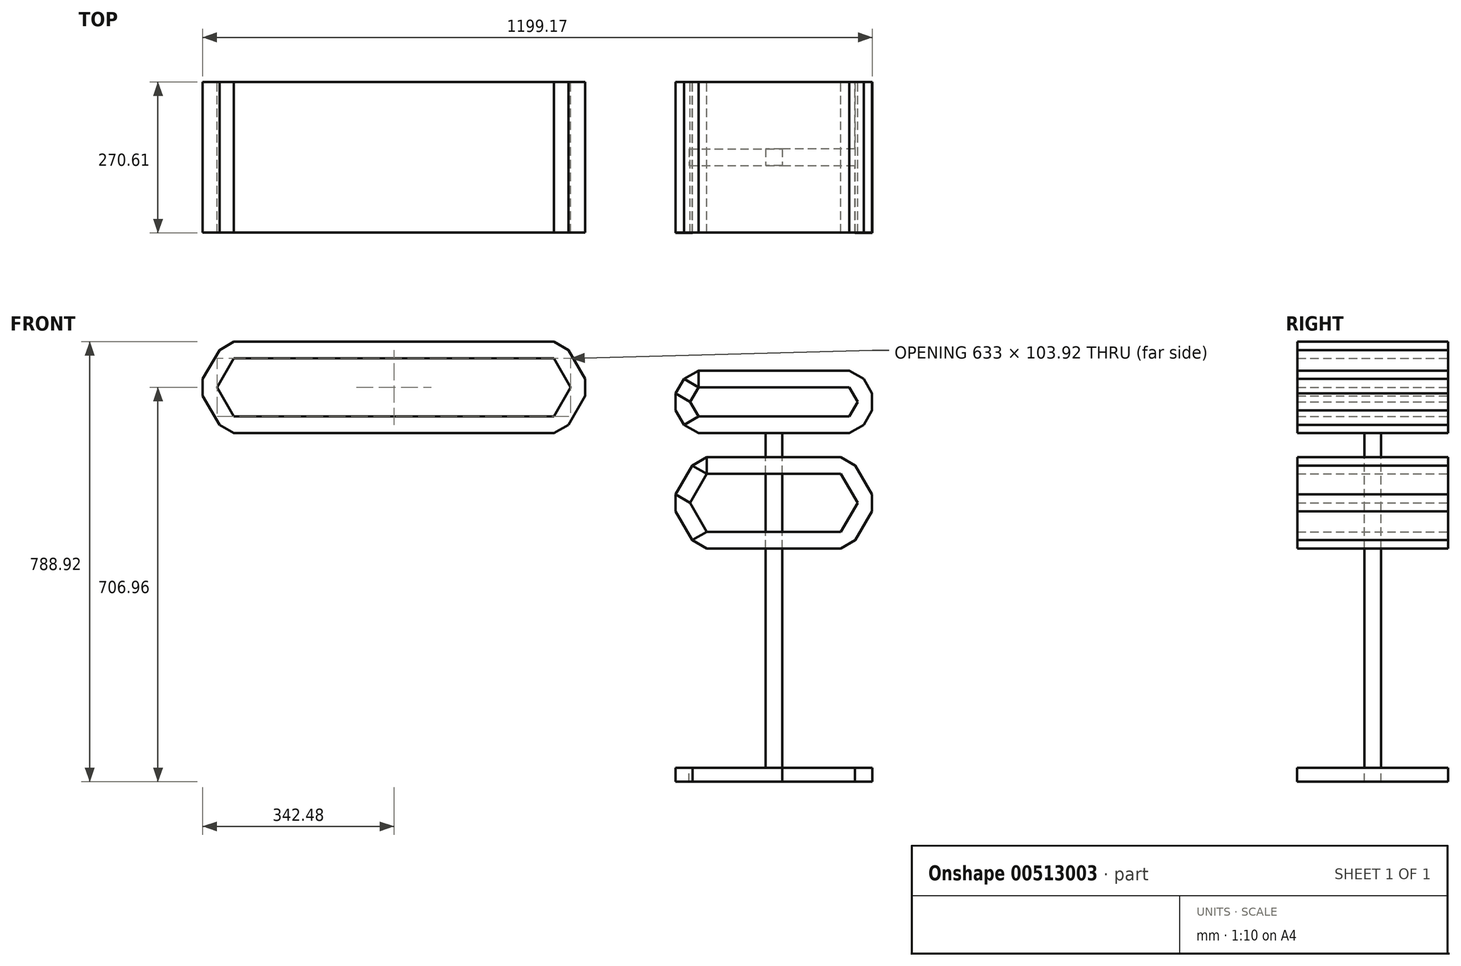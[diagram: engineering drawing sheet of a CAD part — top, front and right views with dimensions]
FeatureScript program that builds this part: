
annotation { "Feature Type Name" : "Feature", "Feature Type Description" : "" }
export const myFeature = defineFeature(function(context is Context, id is Id, definition is map)
    precondition{}
    {
        {
            var Q0;
            Q0=qCreatedBy(makeId("Front.planeOp"),FACE);
            var sketch = newSketch(context, id + "F0", { "sketchPlane" : qUnion([Q0])});
            skLineSegment(sketch, "E0.0", {"start": v(295.98, -66.96) * mm, "end": v(270, -81.96) * mm});
            skLineSegment(sketch, "E0.3", {"start": v(-10.98, -273.94) * mm, "end": v(-40.98, -221.98) * mm});
            skLineSegment(sketch, "E0.4", {"start": v(-40.98, -221.98) * mm, "end": v(-40.98, -191.98) * mm});
            skLineSegment(sketch, "E0.5", {"start": v(-40.98, -10.98) * mm, "end": v(-25.98, 15) * mm});
            skLineSegment(sketch, "E0.6", {"start": v(-10.98, -140.02) * mm, "end": v(15, -125.02) * mm});
            skLineSegment(sketch, "E0.9", {"start": v(295.98, 15) * mm, "end": v(310.98, -10.98) * mm});
            skLineSegment(sketch, "E0.10", {"start": v(310.98, -10.98) * mm, "end": v(310.98, -40.98) * mm});
            skLineSegment(sketch, "E0.11", {"start": v(310.98, -40.98) * mm, "end": v(295.98, -66.96) * mm});
            skLineSegment(sketch, "E1.bottom", {"start": v(-25.98, 15) * mm, "end": v(0, 0) * mm});
            skLineSegment(sketch, "E1.top", {"start": v(-40.98, -10.98) * mm, "end": v(-15, -25.98) * mm});
            skLineSegment(sketch, "E1.left", {"start": v(-10.98, -140.02) * mm, "end": v(-40.98, -191.98) * mm});
            skLineSegment(sketch, "E1.right", {"start": v(0, 0) * mm, "end": v(-15, -25.98) * mm});
            skLineSegment(sketch, "E2", {"start": v(0, 0) * mm, "end": v(0, 30) * mm});
            skLineSegment(sketch, "E3", {"start": v(270, 0) * mm, "end": v(270, 30) * mm});
            skLineSegment(sketch, "E4", {"start": v(270, 0) * mm, "end": v(295.98, 15) * mm});
            skLineSegment(sketch, "E5", {"start": v(270, 0) * mm, "end": v(285, -25.98) * mm});
            skLineSegment(sketch, "E6", {"start": v(310.98, -10.98) * mm, "end": v(285, -25.98) * mm});
            skLineSegment(sketch, "E7", {"start": v(285, -25.98) * mm, "end": v(310.98, -40.98) * mm});
            skLineSegment(sketch, "E8", {"start": v(285, -25.98) * mm, "end": v(270, -51.96) * mm});
            skLineSegment(sketch, "E9", {"start": v(270, -51.96) * mm, "end": v(295.98, -66.96) * mm});
            skLineSegment(sketch, "E10", {"start": v(270, -51.96) * mm, "end": v(270, -81.96) * mm});
            skLineSegment(sketch, "E11", {"start": v(0, -51.96) * mm, "end": v(0, -81.96) * mm});
            skLineSegment(sketch, "E12", {"start": v(0, -51.96) * mm, "end": v(-25.98, -66.96) * mm});
            skLineSegment(sketch, "E13", {"start": v(-40.98, -40.98) * mm, "end": v(-15, -25.98) * mm});
            skLineSegment(sketch, "E14", {"start": v(-15, -25.98) * mm, "end": v(0, -51.96) * mm});
            skLineSegment(sketch, "E15.0", {"start": v(270, -51.96) * mm, "end": v(295.98, -66.96) * mm, "construction": true});
            skLineSegment(sketch, "E16.0", {"start": v(-40.98, -10.98) * mm, "end": v(-15, -25.98) * mm, "construction": true});
            skLineSegment(sketch, "E17", {"start": v(270, 30) * mm, "end": v(295.98, 15) * mm});
            skLineSegment(sketch, "E18", {"start": v(-10.98, -273.94) * mm, "end": v(15, -288.94) * mm});
            skLineSegment(sketch, "E19", {"start": v(0, -81.96) * mm, "end": v(270, -81.96) * mm});
            skLineSegment(sketch, "E20", {"start": v(0, 0) * mm, "end": v(270, 0) * mm});
            skLineSegment(sketch, "E21", {"start": v(270, 30) * mm, "end": v(0, 30) * mm});
            skLineSegment(sketch, "E22", {"start": v(270, -51.96) * mm, "end": v(240, -51.96) * mm});
            skLineSegment(sketch, "E23", {"start": v(240, -51.96) * mm, "end": v(210, -51.96) * mm});
            skLineSegment(sketch, "E24", {"start": v(210, -51.96) * mm, "end": v(180, -51.96) * mm});
            skLineSegment(sketch, "E25", {"start": v(180, -51.96) * mm, "end": v(150, -51.96) * mm});
            skLineSegment(sketch, "E26", {"start": v(150, -51.96) * mm, "end": v(120, -51.96) * mm});
            skLineSegment(sketch, "E27", {"start": v(120, -51.96) * mm, "end": v(90, -51.96) * mm});
            skLineSegment(sketch, "E28", {"start": v(90, -51.96) * mm, "end": v(60, -51.96) * mm});
            skLineSegment(sketch, "E29", {"start": v(60, -51.96) * mm, "end": v(30, -51.96) * mm});
            skLineSegment(sketch, "E30", {"start": v(30, -51.96) * mm, "end": v(0, -51.96) * mm});
            skLineSegment(sketch, "E31.bottom", {"start": v(120, -51.96) * mm, "end": v(120, -51.96) * mm});
            skLineSegment(sketch, "E31.top", {"start": v(120, -81.96) * mm, "end": v(120, -81.96) * mm});
            skLineSegment(sketch, "E31.left", {"start": v(120, -51.96) * mm, "end": v(120, -81.96) * mm});
            skLineSegment(sketch, "E31.right", {"start": v(120, -51.96) * mm, "end": v(120, -81.96) * mm});
            skLineSegment(sketch, "E32.bottom", {"start": v(150, -51.96) * mm, "end": v(150, -51.96) * mm});
            skLineSegment(sketch, "E32.top", {"start": v(150, -81.96) * mm, "end": v(150, -81.96) * mm});
            skLineSegment(sketch, "E32.left", {"start": v(150, -51.96) * mm, "end": v(150, -81.96) * mm});
            skLineSegment(sketch, "E32.right", {"start": v(150, -51.96) * mm, "end": v(150, -81.96) * mm});
            skLineSegment(sketch, "E33", {"start": v(120, -66.96) * mm, "end": v(150, -66.96) * mm});
            skLineSegment(sketch, "E34.top", {"start": v(120, -81.96) * mm, "end": v(150, -81.96) * mm});
            skLineSegment(sketch, "E35", {"start": v(135, -81.96) * mm, "end": v(135, -389.53) * mm});
            skLineSegment(sketch, "E36", {"start": v(-40.98, -191.98) * mm, "end": v(-15, -206.98) * mm});
            skLineSegment(sketch, "E37", {"start": v(-10.98, -140.02) * mm, "end": v(15, -155.02) * mm});
            skLineSegment(sketch, "E38", {"start": v(15, -155.02) * mm, "end": v(15, -125.02) * mm});
            skLineSegment(sketch, "E39", {"start": v(15, -155.02) * mm, "end": v(-15, -206.98) * mm});
            skLineSegment(sketch, "E40", {"start": v(-40.98, -221.98) * mm, "end": v(-15, -206.98) * mm});
            skLineSegment(sketch, "E41", {"start": v(-10.98, -273.94) * mm, "end": v(15, -258.94) * mm});
            skLineSegment(sketch, "E42", {"start": v(15, -288.94) * mm, "end": v(15, -258.94) * mm});
            skLineSegment(sketch, "E43", {"start": v(15, -258.94) * mm, "end": v(-15, -206.98) * mm});
            skLineSegment(sketch, "E44", {"start": v(0, 30) * mm, "end": v(-25.98, 15) * mm});
            skLineSegment(sketch, "E45", {"start": v(-40.98, -10.98) * mm, "end": v(-40.98, -40.98) * mm});
            skLineSegment(sketch, "E46", {"start": v(-40.98, -40.98) * mm, "end": v(-25.98, -66.96) * mm});
            skLineSegment(sketch, "E47", {"start": v(-25.98, -66.96) * mm, "end": v(0, -81.96) * mm});
            skLineSegment(sketch, "E48.MirrorCS", {"start": v(280.98, -140.02) * mm, "end": v(255, -125.02) * mm});
            skLineSegment(sketch, "E49.MirrorCS", {"start": v(255, -155.02) * mm, "end": v(255, -125.02) * mm});
            skLineSegment(sketch, "E50.MirrorCS", {"start": v(255, -258.94) * mm, "end": v(285, -206.98) * mm});
            skLineSegment(sketch, "E51.MirrorCS", {"start": v(280.98, -273.94) * mm, "end": v(255, -258.94) * mm});
            skLineSegment(sketch, "E52.MirrorCS", {"start": v(280.98, -140.02) * mm, "end": v(255, -155.02) * mm});
            skLineSegment(sketch, "E53.MirrorCS", {"start": v(310.98, -221.98) * mm, "end": v(285, -206.98) * mm});
            skLineSegment(sketch, "E54.MirrorCS", {"start": v(310.98, -191.98) * mm, "end": v(285, -206.98) * mm});
            skLineSegment(sketch, "E55.MirrorCS", {"start": v(280.98, -273.94) * mm, "end": v(255, -288.94) * mm});
            skLineSegment(sketch, "E56.MirrorCS", {"start": v(280.98, -273.94) * mm, "end": v(310.98, -221.98) * mm});
            skLineSegment(sketch, "E57.MirrorCS", {"start": v(280.98, -140.02) * mm, "end": v(310.98, -191.98) * mm});
            skLineSegment(sketch, "E58.MirrorCS", {"start": v(255, -288.94) * mm, "end": v(255, -258.94) * mm});
            skLineSegment(sketch, "E59.MirrorCS", {"start": v(310.98, -221.98) * mm, "end": v(310.98, -191.98) * mm});
            skLineSegment(sketch, "E60.MirrorCS", {"start": v(255, -155.02) * mm, "end": v(285, -206.98) * mm});
            skLineSegment(sketch, "E61", {"start": v(15, -155.02) * mm, "end": v(255, -155.02) * mm});
            skLineSegment(sketch, "E62", {"start": v(15, -125.02) * mm, "end": v(255, -125.02) * mm});
            skLineSegment(sketch, "E63", {"start": v(15, -258.94) * mm, "end": v(255, -258.94) * mm});
            skLineSegment(sketch, "E64", {"start": v(15, -288.94) * mm, "end": v(255, -288.94) * mm});
            skLineSegment(sketch, "E65.3", {"start": v(-857.98, -66.96) * mm, "end": v(-887.98, -15) * mm});
            skLineSegment(sketch, "E65.4", {"start": v(-887.98, -15) * mm, "end": v(-887.98, 15) * mm});
            skLineSegment(sketch, "E65.6", {"start": v(-857.98, 66.96) * mm, "end": v(-832, 81.96) * mm});
            skLineSegment(sketch, "E66.left", {"start": v(-857.98, 66.96) * mm, "end": v(-887.98, 15) * mm});
            skLineSegment(sketch, "E67", {"start": v(-857.98, -66.96) * mm, "end": v(-832, -81.96) * mm});
            skLineSegment(sketch, "E68", {"start": v(-887.98, 15) * mm, "end": v(-862, 0) * mm});
            skLineSegment(sketch, "E69", {"start": v(-857.98, 66.96) * mm, "end": v(-832, 51.96) * mm});
            skLineSegment(sketch, "E70", {"start": v(-832, 51.96) * mm, "end": v(-832, 81.96) * mm});
            skLineSegment(sketch, "E71", {"start": v(-832, 51.96) * mm, "end": v(-862, 0) * mm});
            skLineSegment(sketch, "E72", {"start": v(-887.98, -15) * mm, "end": v(-862, 0) * mm});
            skLineSegment(sketch, "E73", {"start": v(-857.98, -66.96) * mm, "end": v(-832, -51.96) * mm});
            skLineSegment(sketch, "E74", {"start": v(-832, -81.96) * mm, "end": v(-832, -51.96) * mm});
            skLineSegment(sketch, "E75", {"start": v(-832, -51.96) * mm, "end": v(-862, 0) * mm});
            skLineSegment(sketch, "E76.MirrorCS", {"start": v(-233.02, 66.96) * mm, "end": v(-259, 81.96) * mm});
            skLineSegment(sketch, "E77.MirrorCS", {"start": v(-259, 51.96) * mm, "end": v(-259, 81.96) * mm});
            skLineSegment(sketch, "E78.MirrorCS", {"start": v(-259, -51.96) * mm, "end": v(-229, 0) * mm});
            skLineSegment(sketch, "E79.MirrorCS", {"start": v(-233.02, -66.96) * mm, "end": v(-259, -51.96) * mm});
            skLineSegment(sketch, "E80.MirrorCS", {"start": v(-233.02, 66.96) * mm, "end": v(-259, 51.96) * mm});
            skLineSegment(sketch, "E81.MirrorCS", {"start": v(-203.02, -15) * mm, "end": v(-229, 0) * mm});
            skLineSegment(sketch, "E82.MirrorCS", {"start": v(-203.02, 15) * mm, "end": v(-229, 0) * mm});
            skLineSegment(sketch, "E83.MirrorCS", {"start": v(-233.02, -66.96) * mm, "end": v(-259, -81.96) * mm});
            skLineSegment(sketch, "E84.MirrorCS", {"start": v(-233.02, -66.96) * mm, "end": v(-203.02, -15) * mm});
            skLineSegment(sketch, "E85.MirrorCS", {"start": v(-233.02, 66.96) * mm, "end": v(-203.02, 15) * mm});
            skLineSegment(sketch, "E86.MirrorCS", {"start": v(-259, -81.96) * mm, "end": v(-259, -51.96) * mm});
            skLineSegment(sketch, "E87.MirrorCS", {"start": v(-203.02, -15) * mm, "end": v(-203.02, 15) * mm});
            skLineSegment(sketch, "E88.MirrorCS", {"start": v(-259, 51.96) * mm, "end": v(-229, 0) * mm});
            skLineSegment(sketch, "E89", {"start": v(-259, 81.96) * mm, "end": v(-832, 81.96) * mm});
            skLineSegment(sketch, "E90", {"start": v(-832, 51.96) * mm, "end": v(-259, 51.96) * mm});
            skLineSegment(sketch, "E91", {"start": v(-832, -51.96) * mm, "end": v(-259, -51.96) * mm});
            skLineSegment(sketch, "E92", {"start": v(-832, -81.96) * mm, "end": v(-259, -81.96) * mm});
            skSolve(sketch);
        }
        {
            var Q0;
            Q0=qCreatedBy(makeId("Front.planeOp"),FACE);
            var sketch = newSketch(context, id + "F1", { "sketchPlane" : qUnion([Q0])});
            skSolve(sketch);
        }
        {
            var Q0;
            Q0=makeQuery(id+"F0.imprint","IMPRINT",FACE,{"disambiguationData":[TD([[makeQuery(id+"F0.imprint","IMPRINT",EDGE,{"derivedFrom":sQuery(id+"F0.wireOp",EDGE,"E0.0")}),-1.0]])]});
            var Q1;
            Q1=makeQuery(id+"F0.imprint","IMPRINT",FACE,{"disambiguationData":[TD([[makeQuery(id+"F0.imprint","IMPRINT",EDGE,{"derivedFrom":sQuery(id+"F0.wireOp",EDGE,"E3")}),-1.0]])]});
            var Q2;
            {var subQ4=sQuery(id+"F0.wireOp",EDGE,"E10");Q2=makeQuery(id+"F0.imprint","IMPRINT",FACE,{"disambiguationData":[TD([[makeQuery(id+"F0.imprint","IMPRINT",EDGE,{"derivedFrom":subQ4}),-1.0]])]});}
            var Q3;
            {var subQ0=sQuery(id+"F0.wireOp",EDGE,"E26");Q3=makeQuery(id+"F0.imprint","IMPRINT",FACE,{"disambiguationData":[TD([[makeQuery(id+"F0.imprint","IMPRINT",EDGE,{"derivedFrom":subQ0}),1.0]])]});}
            var Q4;
            Q4=makeQuery(id+"F0.imprint","IMPRINT",FACE,{"disambiguationData":[TD([[makeQuery(id+"F0.imprint","IMPRINT",EDGE,{"derivedFrom":sQuery(id+"F0.wireOp",EDGE,"E0.3")}),-1.0]])]});
            var Q5;
            Q5=makeQuery(id+"F0.imprint","IMPRINT",FACE,{"disambiguationData":[TD([[makeQuery(id+"F0.imprint","IMPRINT",EDGE,{"derivedFrom":sQuery(id+"F0.wireOp",EDGE,"E0.10")}),-1.0]])]});
            var Q6;
            Q6=makeQuery(id+"F0.imprint","IMPRINT",FACE,{"disambiguationData":[TD([[makeQuery(id+"F0.imprint","IMPRINT",EDGE,{"derivedFrom":sQuery(id+"F0.wireOp",EDGE,"E0.4")}),-1.0]])]});
            var Q7;
            {var subQ1=sQuery(id+"F0.wireOp",EDGE,"E11");Q7=makeQuery(id+"F0.imprint","IMPRINT",FACE,{"disambiguationData":[TD([[makeQuery(id+"F0.imprint","IMPRINT",EDGE,{"derivedFrom":subQ1}),1.0]])]});}
            var Q8;
            {var subQ3=sQuery(id+"F0.wireOp",EDGE,"E33");Q8=makeQuery(id+"F0.imprint","IMPRINT",FACE,{"disambiguationData":[TD([[makeQuery(id+"F0.imprint","IMPRINT",EDGE,{"derivedFrom":subQ3}),-1.0]])]});}
            var Q9;
            Q9=makeQuery(id+"F0.imprint","IMPRINT",FACE,{"disambiguationData":[TD([[makeQuery(id+"F0.imprint","IMPRINT",EDGE,{"derivedFrom":sQuery(id+"F0.wireOp",EDGE,"E0.11")}),-1.0]])]});
            var Q10;
            Q10=makeQuery(id+"F0.imprint","IMPRINT",FACE,{"disambiguationData":[TD([[makeQuery(id+"F0.imprint","IMPRINT",EDGE,{"derivedFrom":sQuery(id+"F0.wireOp",EDGE,"E11")}),-1.0]])]});
            var Q11;
            Q11=makeQuery(id+"F0.imprint","IMPRINT",FACE,{"disambiguationData":[TD([[makeQuery(id+"F0.imprint","IMPRINT",EDGE,{"derivedFrom":sQuery(id+"F0.wireOp",EDGE,"E0.9")}),-1.0]])]});
            var Q12;
            Q12=makeQuery(id+"F0.imprint","IMPRINT",FACE,{"disambiguationData":[TD([[makeQuery(id+"F0.imprint","IMPRINT",EDGE,{"derivedFrom":sQuery(id+"F0.wireOp",EDGE,"E2")}),-1.0]])]});
            var Q13;
            Q13=makeQuery(id+"F0.imprint","IMPRINT",FACE,{"disambiguationData":[TD([[makeQuery(id+"F0.imprint","IMPRINT",EDGE,{"derivedFrom":sQuery(id+"F0.wireOp",EDGE,"E1.bottom")}),-1.0]])]});
            var Q14;
            Q14=makeQuery(id+"F0.imprint","IMPRINT",FACE,{"disambiguationData":[TD([[makeQuery(id+"F0.imprint","IMPRINT",EDGE,{"derivedFrom":sQuery(id+"F0.wireOp",EDGE,"E0.6")}),-1.0]])]});
            var Q15;
            Q15 = qSketchRegion(id + "F1", true);
            extrude(context, id + "F2", {"entities" : qUnion([Q0, Q1, Q2, Q3, Q4, Q5, Q6, Q7, Q8, Q9, Q10, Q11, Q12, Q13, Q14, Q15]), "depth" : 270 * mm});
        }
        {
            var Q0;
            Q0=makeQuery(id+"F2.opExtrude","SWEPT_FACE",FACE,{"disambiguationData":[OSD([sQuery(id+"F0.wireOp",EDGE,"E19"),sQuery(id+"F0.wireOp",EDGE,"E34.top")])]});
            var sketch = newSketch(context, id + "F3", { "sketchPlane" : qUnion([Q0])});
            skPoint(sketch, "E93.startSnap0", {"position": v(135, 270) * mm});
            skLineSegment(sketch, "E94.bottom", {"start": v(150, 120) * mm, "end": v(120, 120) * mm});
            skLineSegment(sketch, "E94.top", {"start": v(150, 150) * mm, "end": v(120, 150) * mm});
            skLineSegment(sketch, "E94.left", {"start": v(150, 120) * mm, "end": v(150, 150) * mm});
            skLineSegment(sketch, "E94.right", {"start": v(120, 120) * mm, "end": v(120, 150) * mm});
            skPoint(sketch, "E94.middle", {"position": v(135, 135) * mm});
            skSolve(sketch);
        }
        {
            var Q0;
            Q0=makeQuery(id+"F3.imprint","IMPRINT",FACE,{"disambiguationData":[TD([[makeQuery(id+"F3.imprint","IMPRINT",EDGE,{"derivedFrom":sQuery(id+"F3.wireOp",EDGE,"E94.bottom")}),-1.0]])]});
            extrude(context, id + "F4", {"entities" : qUnion([Q0]), "operationType" : NewBodyOperationType.ADD, "depth" : 600 * mm});
        }
        {
            var Q0;
            Q0=makeQuery(id+"F4.opExtrude","CAP_FACE",FACE,{"disambiguationData":[OSD([sQuery(id+"F3.wireOp",EDGE,"E94.bottom"),sQuery(id+"F3.wireOp",EDGE,"E94.top"),sQuery(id+"F3.wireOp",EDGE,"E94.left"),sQuery(id+"F3.wireOp",EDGE,"E94.right")])],"isStart":false});
            var sketch = newSketch(context, id + "F5", { "sketchPlane" : qUnion([Q0])});
            skLineSegment(sketch, "E95", {"start": v(120, 150) * mm, "end": v(-41.14, 150) * mm});
            skLineSegment(sketch, "E96", {"start": v(-41.14, 150) * mm, "end": v(-41.14, 270.6) * mm});
            skLineSegment(sketch, "E97", {"start": v(-41.14, 270.6) * mm, "end": v(-10.86, 270.6) * mm});
            skLineSegment(sketch, "E98", {"start": v(-10.86, 270.6) * mm, "end": v(-10.86, 0) * mm});
            skLineSegment(sketch, "E99", {"start": v(-10.86, 0) * mm, "end": v(-41.14, 0) * mm});
            skLineSegment(sketch, "E100", {"start": v(-41.14, 0) * mm, "end": v(-41.14, 150) * mm});
            skLineSegment(sketch, "E101", {"start": v(120, 120) * mm, "end": v(-41.14, 120) * mm});
            skLineSegment(sketch, "E102", {"start": v(-41.14, 120) * mm, "end": v(-41.14, 150) * mm});
            skLineSegment(sketch, "E103", {"start": v(150, 150) * mm, "end": v(311.19, 150) * mm});
            skLineSegment(sketch, "E104", {"start": v(311.19, 150) * mm, "end": v(311.19, 270.6) * mm});
            skLineSegment(sketch, "E105", {"start": v(311.19, 270.6) * mm, "end": v(280, 270.6) * mm});
            skLineSegment(sketch, "E106", {"start": v(280, 270.6) * mm, "end": v(280, 0) * mm});
            skLineSegment(sketch, "E107", {"start": v(280, 0) * mm, "end": v(311.19, 0) * mm});
            skLineSegment(sketch, "E108", {"start": v(311.19, 0) * mm, "end": v(311.19, 150) * mm});
            skLineSegment(sketch, "E109", {"start": v(311.19, 120) * mm, "end": v(150, 120) * mm});
            skLineSegment(sketch, "E110", {"start": v(150, 120) * mm, "end": v(150, 150) * mm});
            skSolve(sketch);
        }
        {
            var Q0;
            Q0 = qSketchRegion(id + "F5", true);
            extrude(context, id + "F6", {"entities" : qUnion([Q0]), "depth" : 25 * mm});
        }
        {
            var Q0;
            Q0=makeQuery(id+"F6.opExtrude","SWEPT_FACE",FACE,{"disambiguationData":[OSD([sQuery(id+"F5.wireOp",EDGE,"E110")])]});
            extrude(context, id + "F7", {"entities" : qUnion([Q0]), "depth" : 167 * mm});
        }
        {
            var Q0;
            Q0=makeQuery(id+"F0.imprint","IMPRINT",FACE,{"disambiguationData":[TD([[makeQuery(id+"F0.imprint","IMPRINT",EDGE,{"derivedFrom":sQuery(id+"F0.wireOp",EDGE,"E1.bottom")}),1.0]])]});
            var Q1;
            Q1=makeQuery(id+"F0.imprint","IMPRINT",FACE,{"disambiguationData":[TD([[makeQuery(id+"F0.imprint","IMPRINT",EDGE,{"derivedFrom":sQuery(id+"F0.wireOp",EDGE,"E1.top")}),-1.0]])]});
            var Q2;
            Q2=makeQuery(id+"F0.imprint","IMPRINT",FACE,{"disambiguationData":[TD([[makeQuery(id+"F0.imprint","IMPRINT",EDGE,{"derivedFrom":sQuery(id+"F0.wireOp",EDGE,"E12")}),-1.0]])]});
            extrude(context, id + "F8", {"entities" : qUnion([Q0, Q1, Q2]), "depth" : 270 * mm});
        }
        {
            var Q0;
            {var subQ5=sQuery(id+"F0.wireOp",EDGE,"E38");Q0=makeQuery(id+"F0.imprint","IMPRINT",FACE,{"disambiguationData":[TD([[makeQuery(id+"F0.imprint","IMPRINT",EDGE,{"derivedFrom":subQ5}),-1.0]])]});}
            var Q1;
            {var subQ5=sQuery(id+"F0.wireOp",EDGE,"E49.MirrorCS");Q1=makeQuery(id+"F0.imprint","IMPRINT",FACE,{"disambiguationData":[TD([[makeQuery(id+"F0.imprint","IMPRINT",EDGE,{"derivedFrom":subQ5}),1.0]])]});}
            var Q2;
            Q2=makeQuery(id+"F0.imprint","IMPRINT",FACE,{"disambiguationData":[TD([[makeQuery(id+"F0.imprint","IMPRINT",EDGE,{"derivedFrom":sQuery(id+"F0.wireOp",EDGE,"E48.MirrorCS")}),1.0]])]});
            var Q3;
            Q3=makeQuery(id+"F0.imprint","IMPRINT",FACE,{"disambiguationData":[TD([[makeQuery(id+"F0.imprint","IMPRINT",EDGE,{"derivedFrom":sQuery(id+"F0.wireOp",EDGE,"E52.MirrorCS")}),1.0]])]});
            var Q4;
            Q4=makeQuery(id+"F0.imprint","IMPRINT",FACE,{"disambiguationData":[TD([[makeQuery(id+"F0.imprint","IMPRINT",EDGE,{"derivedFrom":sQuery(id+"F0.wireOp",EDGE,"E50.MirrorCS")}),-1.0]])]});
            var Q5;
            {var subQ5=sQuery(id+"F0.wireOp",EDGE,"E58.MirrorCS");Q5=makeQuery(id+"F0.imprint","IMPRINT",FACE,{"disambiguationData":[TD([[makeQuery(id+"F0.imprint","IMPRINT",EDGE,{"derivedFrom":subQ5}),1.0]])]});}
            var Q6;
            {var subQ5=sQuery(id+"F0.wireOp",EDGE,"E42");Q6=makeQuery(id+"F0.imprint","IMPRINT",FACE,{"disambiguationData":[TD([[makeQuery(id+"F0.imprint","IMPRINT",EDGE,{"derivedFrom":subQ5}),-1.0]])]});}
            var Q7;
            Q7=makeQuery(id+"F0.imprint","IMPRINT",FACE,{"disambiguationData":[TD([[makeQuery(id+"F0.imprint","IMPRINT",EDGE,{"derivedFrom":sQuery(id+"F0.wireOp",EDGE,"E1.left")}),1.0]])]});
            var Q8;
            Q8=makeQuery(id+"F0.imprint","IMPRINT",FACE,{"disambiguationData":[TD([[makeQuery(id+"F0.imprint","IMPRINT",EDGE,{"derivedFrom":sQuery(id+"F0.wireOp",EDGE,"E18")}),1.0]])]});
            var Q9;
            Q9=makeQuery(id+"F0.imprint","IMPRINT",FACE,{"disambiguationData":[TD([[makeQuery(id+"F0.imprint","IMPRINT",EDGE,{"derivedFrom":sQuery(id+"F0.wireOp",EDGE,"E51.MirrorCS")}),1.0]])]});
            var Q10;
            Q10=makeQuery(id+"F0.imprint","IMPRINT",FACE,{"disambiguationData":[TD([[makeQuery(id+"F0.imprint","IMPRINT",EDGE,{"derivedFrom":sQuery(id+"F0.wireOp",EDGE,"E53.MirrorCS")}),-1.0]])]});
            extrude(context, id + "F9", {"entities" : qUnion([Q0, Q1, Q2, Q3, Q4, Q5, Q6, Q7, Q8, Q9, Q10]), "depth" : 270 * mm});
        }
        {
            var Q0;
            Q0=makeQuery(id+"F0.imprint","IMPRINT",FACE,{"disambiguationData":[TD([[makeQuery(id+"F0.imprint","IMPRINT",EDGE,{"derivedFrom":sQuery(id+"F0.wireOp",EDGE,"E65.4")}),-1.0]])]});
            var Q1;
            Q1=makeQuery(id+"F0.imprint","IMPRINT",FACE,{"disambiguationData":[TD([[makeQuery(id+"F0.imprint","IMPRINT",EDGE,{"derivedFrom":sQuery(id+"F0.wireOp",EDGE,"E65.6")}),-1.0]])]});
            var Q2;
            Q2=makeQuery(id+"F0.imprint","IMPRINT",FACE,{"disambiguationData":[TD([[makeQuery(id+"F0.imprint","IMPRINT",EDGE,{"derivedFrom":sQuery(id+"F0.wireOp",EDGE,"E67")}),1.0]])]});
            var Q3;
            Q3=makeQuery(id+"F0.imprint","IMPRINT",FACE,{"disambiguationData":[TD([[makeQuery(id+"F0.imprint","IMPRINT",EDGE,{"derivedFrom":sQuery(id+"F0.wireOp",EDGE,"E76.MirrorCS")}),1.0]])]});
            var Q4;
            Q4=makeQuery(id+"F0.imprint","IMPRINT",FACE,{"disambiguationData":[TD([[makeQuery(id+"F0.imprint","IMPRINT",EDGE,{"derivedFrom":sQuery(id+"F0.wireOp",EDGE,"E79.MirrorCS")}),1.0]])]});
            var Q5;
            Q5=makeQuery(id+"F0.imprint","IMPRINT",FACE,{"disambiguationData":[TD([[makeQuery(id+"F0.imprint","IMPRINT",EDGE,{"derivedFrom":sQuery(id+"F0.wireOp",EDGE,"E81.MirrorCS")}),-1.0]])]});
            var Q6;
            Q6=makeQuery(id+"F0.imprint","IMPRINT",FACE,{"disambiguationData":[TD([[makeQuery(id+"F0.imprint","IMPRINT",EDGE,{"derivedFrom":sQuery(id+"F0.wireOp",EDGE,"E65.3")}),-1.0]])]});
            var Q7;
            Q7=makeQuery(id+"F0.imprint","IMPRINT",FACE,{"disambiguationData":[TD([[makeQuery(id+"F0.imprint","IMPRINT",EDGE,{"derivedFrom":sQuery(id+"F0.wireOp",EDGE,"E66.left")}),1.0]])]});
            var Q8;
            Q8=makeQuery(id+"F0.imprint","IMPRINT",FACE,{"disambiguationData":[TD([[makeQuery(id+"F0.imprint","IMPRINT",EDGE,{"derivedFrom":sQuery(id+"F0.wireOp",EDGE,"E74")}),-1.0]])]});
            var Q9;
            Q9=makeQuery(id+"F0.imprint","IMPRINT",FACE,{"disambiguationData":[TD([[makeQuery(id+"F0.imprint","IMPRINT",EDGE,{"derivedFrom":sQuery(id+"F0.wireOp",EDGE,"E78.MirrorCS")}),-1.0]])]});
            var Q10;
            Q10=makeQuery(id+"F0.imprint","IMPRINT",FACE,{"disambiguationData":[TD([[makeQuery(id+"F0.imprint","IMPRINT",EDGE,{"derivedFrom":sQuery(id+"F0.wireOp",EDGE,"E80.MirrorCS")}),1.0]])]});
            var Q11;
            Q11=makeQuery(id+"F0.imprint","IMPRINT",FACE,{"disambiguationData":[TD([[makeQuery(id+"F0.imprint","IMPRINT",EDGE,{"derivedFrom":sQuery(id+"F0.wireOp",EDGE,"E70")}),-1.0]])]});
            extrude(context, id + "F10", {"entities" : qUnion([Q0, Q1, Q2, Q3, Q4, Q5, Q6, Q7, Q8, Q9, Q10, Q11]), "depth" : 270 * mm, "offsetDistance" : 25 * mm});
        }
    });
